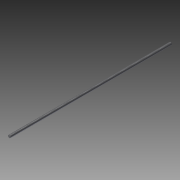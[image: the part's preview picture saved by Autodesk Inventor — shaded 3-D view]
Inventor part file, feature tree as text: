
AUTODESK INVENTOR PART (.ipt)
format: ipt  version: 2015 (Build 190159000, 159)  size: 71,680 bytes
history: native  units: mm
features: extrude x1, thread x1, sketch x1
ambient origin geometry x8: Origin, YZ Plane, XZ Plane, XY Plane, X Axis, Y Axis, Z Axis, Center Point
bodies: Solid1 (feature_tree)
feature tree (3):
  extrude  "Extrusion1"  Depth=300.0mm TaperAngle=0.0deg
  thread  "Thread1"  [1 undecoded]
  sketch  "Sketch1"  dims[d0=5.0mm d1=300.0mm d2=0.0mm d3=10.0mm d4=0.0mm]
note: 1 required parameter value undecoded (feature->parameter linkage not recoverable at this tier; creation-order binding heuristic only, values carry confidence <= 0.55)
